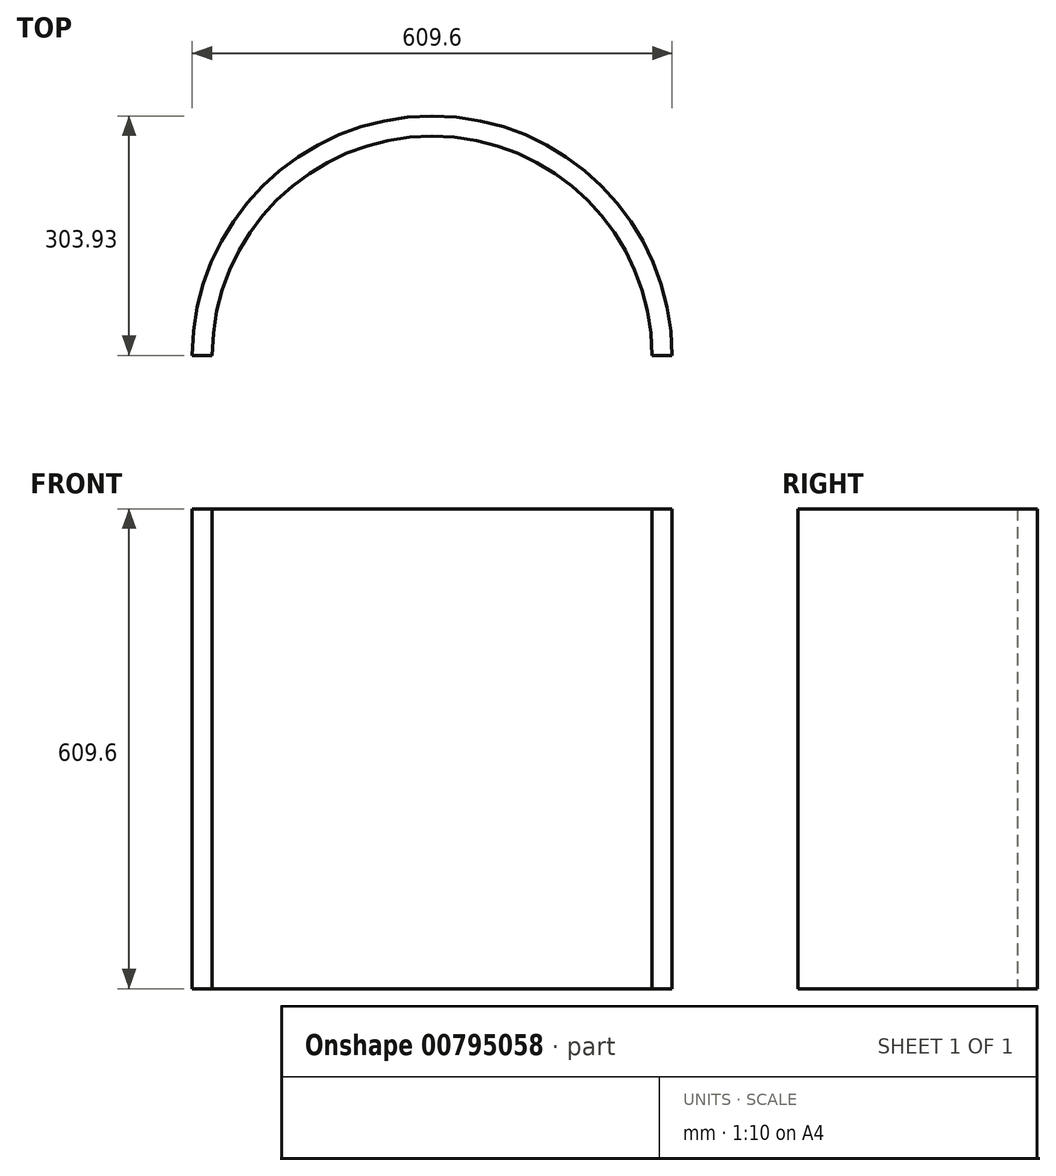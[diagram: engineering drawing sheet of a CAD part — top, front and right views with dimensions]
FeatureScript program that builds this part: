
annotation { "Feature Type Name" : "Feature", "Feature Type Description" : "" }
export const myFeature = defineFeature(function(context is Context, id is Id, definition is map)
    precondition{}
    {
        {
            var Q0;
            Q0=qCreatedBy(makeId("Top.planeOp"),FACE);
            var sketch = newSketch(context, id + "F0", { "sketchPlane" : qUnion([Q0])});
            skLineSegment(sketch, "E0", {"start": v(0, 0) * mm, "end": v(-304.8, 0) * mm, "construction": true});
            skLineSegment(sketch, "E1", {"start": v(0, -9.15) * mm, "end": v(-279.4, -9.15) * mm, "construction": true});
            skLineSegment(sketch, "E2.MirrorCS", {"start": v(0, 0) * mm, "end": v(304.8, 0) * mm, "construction": true});
            skLineSegment(sketch, "E3.MirrorCS", {"start": v(0, -9.15) * mm, "end": v(279.4, -9.15) * mm, "construction": true});
            skArc(sketch, "E4", {"start": v(279.4, 0) * mm, "mid": v(0, 278.53) * mm, "end": v(-279.4, 0) * mm});
            skArc(sketch, "E5", {"start": v(304.8, 0) * mm, "mid": v(0, 303.93) * mm, "end": v(-304.8, 0) * mm});
            skLineSegment(sketch, "E6", {"start": v(-304.8, 0) * mm, "end": v(-279.4, 0) * mm});
            skLineSegment(sketch, "E7", {"start": v(279.4, 0) * mm, "end": v(304.8, 0) * mm});
            skSolve(sketch);
        }
        {
            var Q0;
            Q0=qSketchRegion(id+"F0",true);
            extrude(context, id + "F1", {"entities" : qUnion([Q0]), "depth" : 609.6 * mm, "offsetDistance" : 25.4 * mm});
        }
    });
